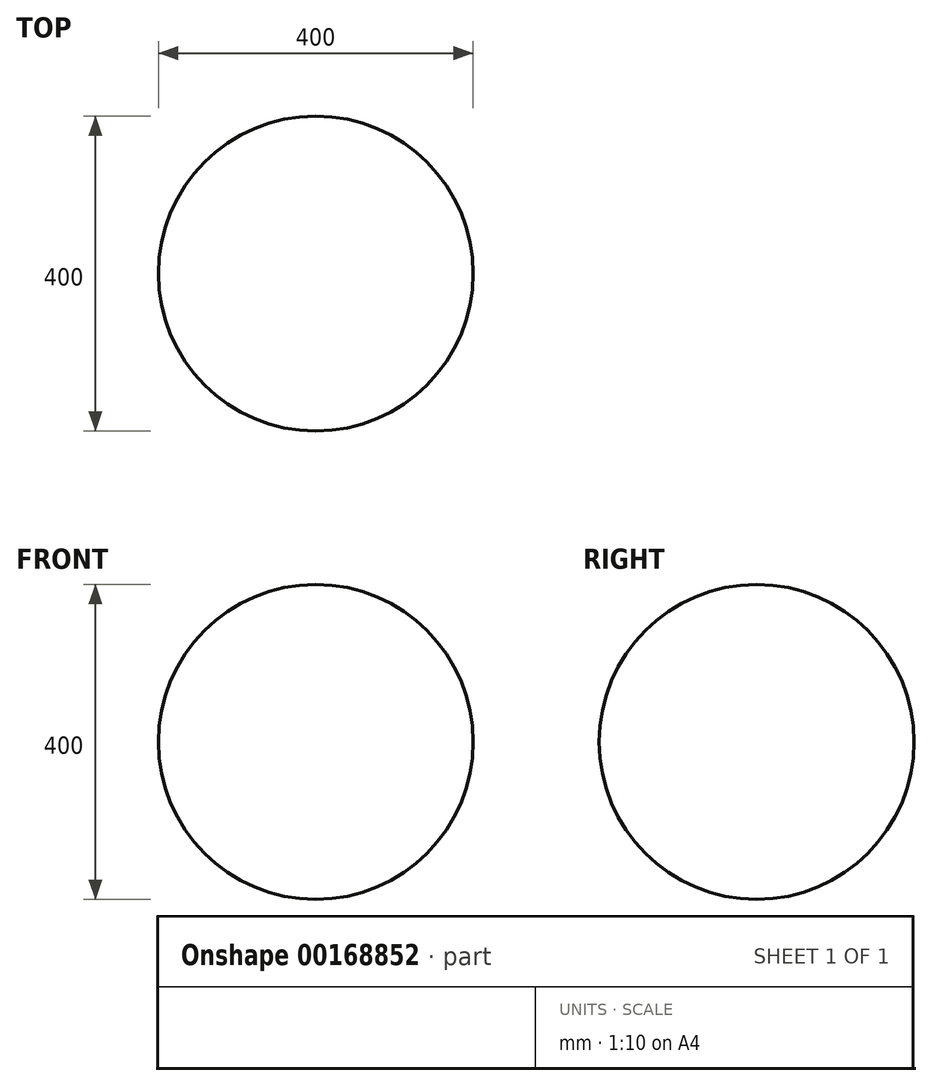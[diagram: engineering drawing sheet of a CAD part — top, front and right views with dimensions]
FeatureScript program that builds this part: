
annotation { "Feature Type Name" : "Feature", "Feature Type Description" : "" }
export const myFeature = defineFeature(function(context is Context, id is Id, definition is map)
    precondition{}
    {
        {
            var Q0;
            Q0=qCreatedBy(makeId("Front.planeOp"),FACE);
            var sketch = newSketch(context, id + "F0", { "sketchPlane" : qUnion([Q0])});
            skLineSegment(sketch, "E0", {"start": v(0, 200) * mm, "end": v(0, -200) * mm});
            skArc(sketch, "E1", {"start": v(0, 200) * mm, "mid": v(-200, 0) * mm, "end": v(0, -200) * mm});
            skSolve(sketch);
        }
        {
            var Q0;
            Q0=makeQuery(id+"F0.imprint","IMPRINT",FACE,{"disambiguationData":[TD([[makeQuery(id+"F0.imprint","IMPRINT",EDGE,{"derivedFrom":sQuery(id+"F0.wireOp",EDGE,"E0")}),-1.0]])]});
            var Q1;
            Q1=sQuery(id+"F0.wireOp",EDGE,"E0");
            revolve(context, id + "F1", {"entities" : qUnion([Q0]), "axis" : qUnion([Q1]), "revolveType" : RevolveType.FULL});
        }
    });
